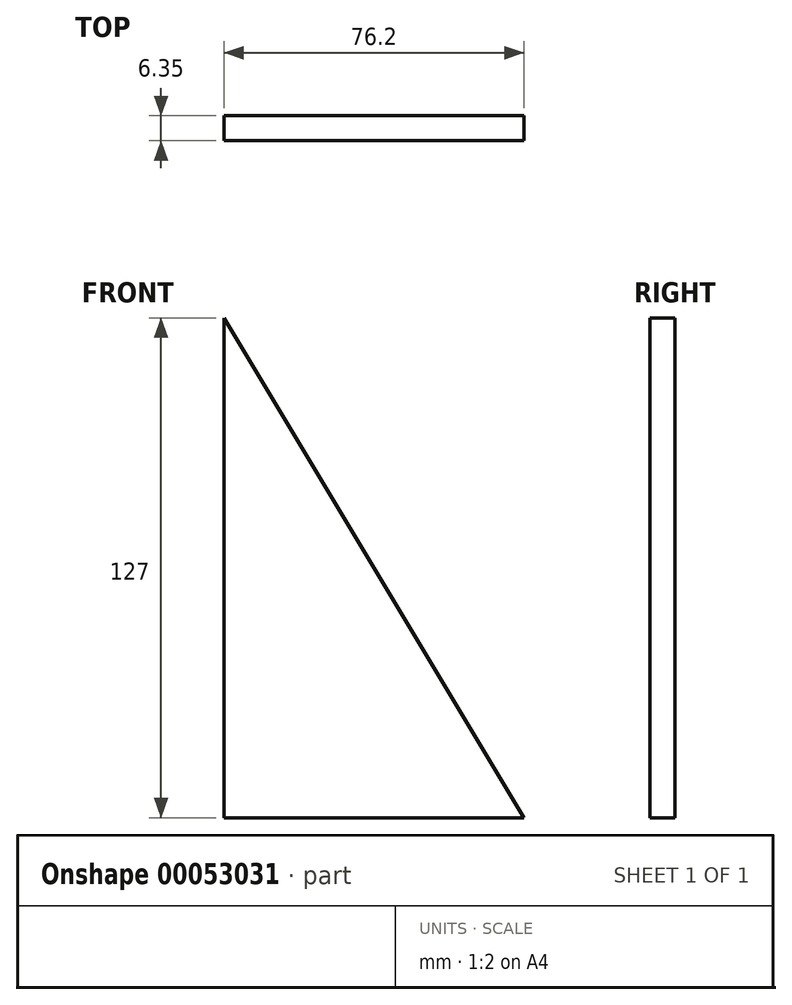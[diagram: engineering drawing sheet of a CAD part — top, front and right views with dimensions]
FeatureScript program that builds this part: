
annotation { "Feature Type Name" : "Feature", "Feature Type Description" : "" }
export const myFeature = defineFeature(function(context is Context, id is Id, definition is map)
    precondition{}
    {
        {
            var Q0;
            Q0=qCreatedBy(makeId("Front.planeOp"),FACE);
            var sketch = newSketch(context, id + "F0", { "sketchPlane" : qUnion([Q0])});
            skLineSegment(sketch, "E0", {"start": v(0, 0) * mm, "end": v(-76.2, 127) * mm});
            skLineSegment(sketch, "E1", {"start": v(-76.2, 127) * mm, "end": v(-76.2, 0) * mm});
            skLineSegment(sketch, "E2", {"start": v(-76.2, 0) * mm, "end": v(0, 0) * mm});
            skSolve(sketch);
        }
        {
            var Q0;
            Q0 = qSketchRegion(id + "F0", true);
            extrude(context, id + "F1", {"entities" : qUnion([Q0]), "depth" : 6.35 * mm});
        }
    });
